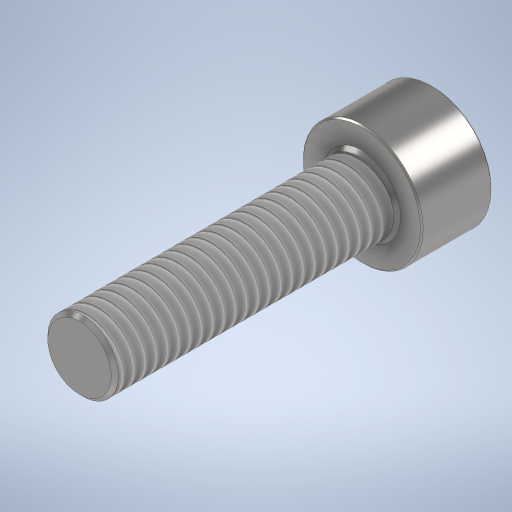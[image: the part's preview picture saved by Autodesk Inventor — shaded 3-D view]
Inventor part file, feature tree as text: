
AUTODESK INVENTOR PART (.ipt)
format: ipt  version: 2024 (Build 280153000, 153)  size: 332,800 bytes
history: native  units: mm
features: extrude x3, chamfer x3, sketch x2, thread x1, hole x1
ambient origin geometry x8: Origin, YZ Plane, XZ Plane, XY Plane, X Axis, Y Axis, Z Axis, Center Point
bodies: Solid1 (feature_tree)
feature tree (10):
  sketch  "Sketch1"  dims[d0=8.5mm d1=5.0mm]
  extrude  "Extrusion1"  Depth=5.0mm
  extrude  "Extrusion2"  Depth=2.5mm TaperAngle=0.0deg
  thread  "Thread1"  [1 undecoded]
  chamfer  "Chamfer1"  Distance=0.1mm Angle=45.0deg
  sketch  "Sketch2"  dims[d2=20.0mm d3=0.0mm d4=5.0mm d5=0.0mm d6=15.0mm d7=0.0mm d8=0.1mm d9=2.0mm d10=45.0deg d11=3.75mm d12=4.0mm d15=0.5mm d16=2.0mm d17=45.0deg d18=3.0mm d19=0.0mm d20=0.25mm d21=2.0mm d22=45.0deg d23=3.75mm d24=6.0mm d25=4.0mm d26=2.0mm d27=90.0deg d28=2.5mm d29=150.0deg]
  hole  "Hole1"  [1 undecoded]
  chamfer  "Chamfer2"  Distance=4.0mm
  extrude  "Extrusion4"  Depth=2.5mm TaperAngle=45.0deg
  chamfer  "Chamfer3"  Distance=3.0mm
note: 2 required parameter values undecoded (feature->parameter linkage not recoverable at this tier; creation-order binding heuristic only, values carry confidence <= 0.55)
